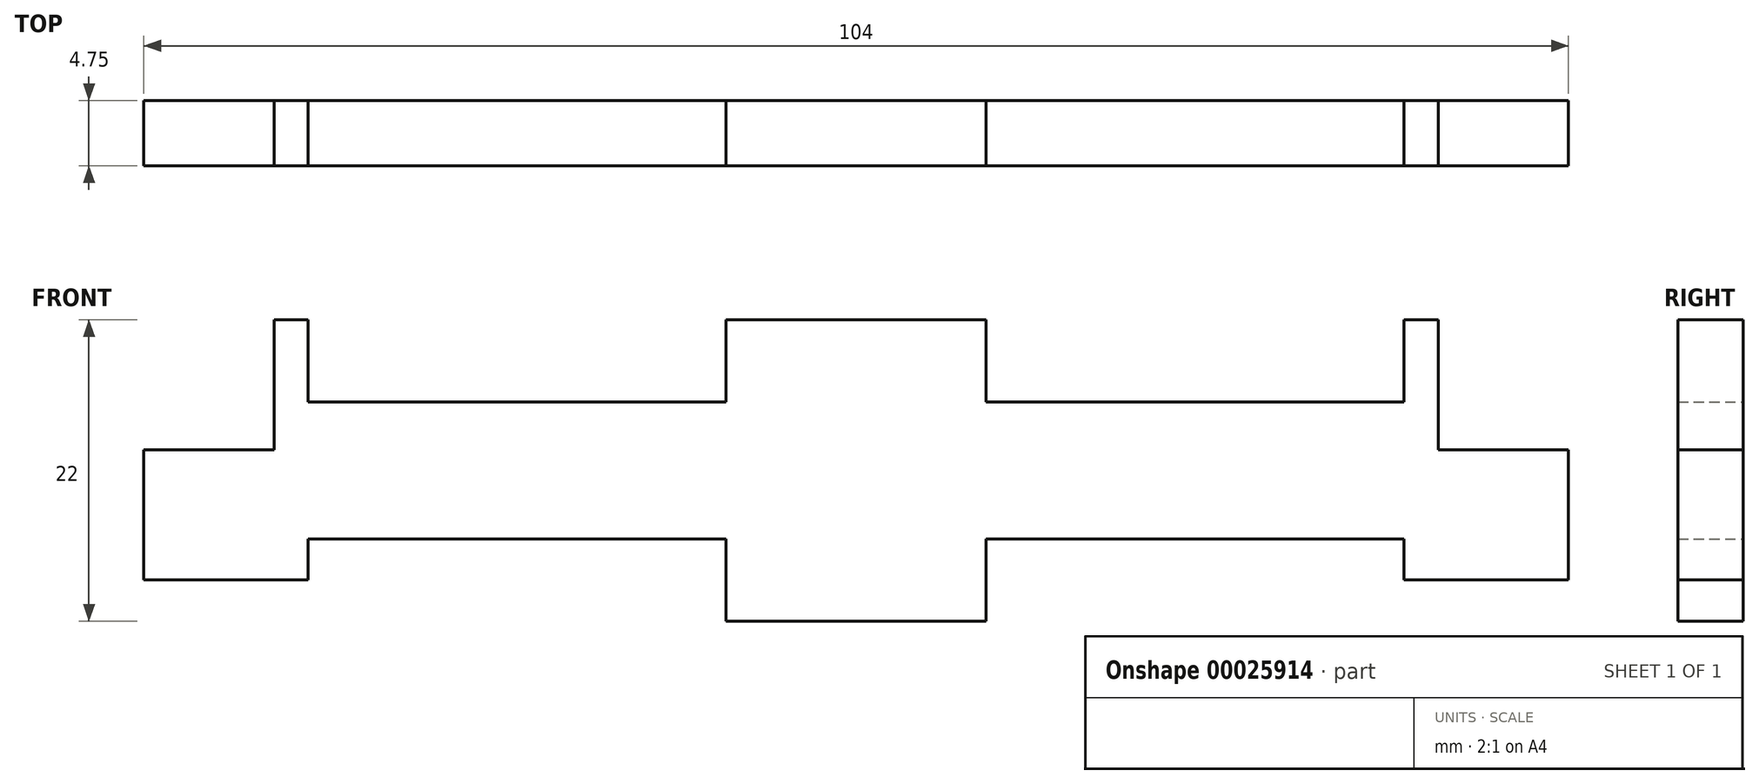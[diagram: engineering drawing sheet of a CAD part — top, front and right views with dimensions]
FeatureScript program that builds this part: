
annotation { "Feature Type Name" : "Feature", "Feature Type Description" : "" }
export const myFeature = defineFeature(function(context is Context, id is Id, definition is map)
    precondition{}
    {
        {
            var Q0;
            Q0=qCreatedBy(makeId("Front.planeOp"),FACE);
            var sketch = newSketch(context, id + "F0", { "sketchPlane" : qUnion([Q0])});
            skLineSegment(sketch, "E0", {"start": v(0, -6) * mm, "end": v(9.5, -6) * mm});
            skLineSegment(sketch, "E1", {"start": v(9.5, -6) * mm, "end": v(9.5, 0) * mm});
            skLineSegment(sketch, "E2", {"start": v(9.5, 0) * mm, "end": v(40, 0) * mm});
            skLineSegment(sketch, "E3", {"start": v(40, 0) * mm, "end": v(40, -3) * mm});
            skLineSegment(sketch, "E4", {"start": v(40, -3) * mm, "end": v(52, -3) * mm});
            skLineSegment(sketch, "E5", {"start": v(52, -3) * mm, "end": v(52, 6.5) * mm});
            skLineSegment(sketch, "E6", {"start": v(52, 6.5) * mm, "end": v(42.5, 6.5) * mm});
            skLineSegment(sketch, "E7", {"start": v(42.5, 6.5) * mm, "end": v(42.5, 16) * mm});
            skLineSegment(sketch, "E8", {"start": v(42.5, 16) * mm, "end": v(40, 16) * mm});
            skLineSegment(sketch, "E9", {"start": v(40, 16) * mm, "end": v(40, 10) * mm});
            skLineSegment(sketch, "E10", {"start": v(40, 10) * mm, "end": v(9.5, 10) * mm});
            skLineSegment(sketch, "E11", {"start": v(9.5, 10) * mm, "end": v(9.5, 16) * mm});
            skLineSegment(sketch, "E12", {"start": v(9.5, 16) * mm, "end": v(0, 16) * mm});
            skLineSegment(sketch, "E13", {"start": v(0, 16) * mm, "end": v(0, -6) * mm});
            skSolve(sketch);
        }
        {
            var Q0;
            Q0=makeQuery(id+"F0.imprint","IMPRINT",FACE,{"disambiguationData":[TD([[makeQuery(id+"F0.imprint","IMPRINT",EDGE,{"derivedFrom":sQuery(id+"F0.wireOp",EDGE,"E0")}),1.0]])]});
            extrude(context, id + "F1", {"entities" : qUnion([Q0]), "depth" : 4.75 * mm});
        }
        {
            var Q0;
            Q0=makeQuery(id+"F1.opExtrude","SWEPT_BODY",BODY,{"disambiguationData":[OSD([sQuery(id+"F0.wireOp",EDGE,"E0"),sQuery(id+"F0.wireOp",EDGE,"E1"),sQuery(id+"F0.wireOp",EDGE,"E2"),sQuery(id+"F0.wireOp",EDGE,"E3"),sQuery(id+"F0.wireOp",EDGE,"E4"),sQuery(id+"F0.wireOp",EDGE,"E5"),sQuery(id+"F0.wireOp",EDGE,"E6"),sQuery(id+"F0.wireOp",EDGE,"E7"),sQuery(id+"F0.wireOp",EDGE,"E8"),sQuery(id+"F0.wireOp",EDGE,"E9"),sQuery(id+"F0.wireOp",EDGE,"E10"),sQuery(id+"F0.wireOp",EDGE,"E11"),sQuery(id+"F0.wireOp",EDGE,"E12"),sQuery(id+"F0.wireOp",EDGE,"E13")])]});
            var Q1;
            Q1=qCreatedBy(makeId("Right.planeOp"),FACE);
            mirror(context, id + "F2", {"operationType" : NewBodyOperationType.ADD, "entities" : qUnion([Q0]), "mirrorPlane" : qUnion([Q1])});
        }
    });
